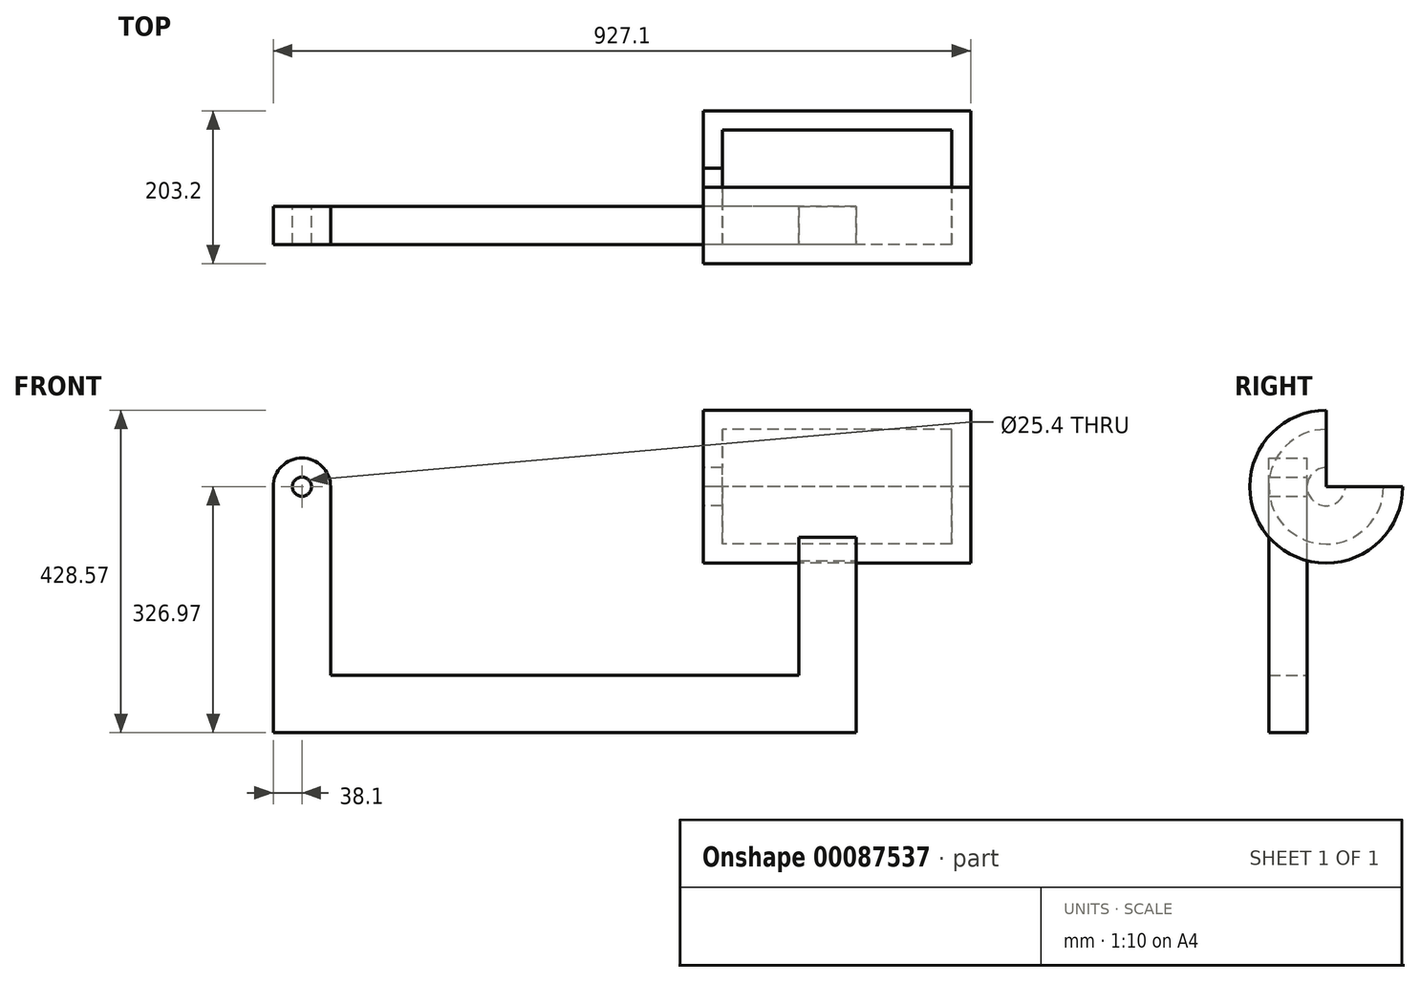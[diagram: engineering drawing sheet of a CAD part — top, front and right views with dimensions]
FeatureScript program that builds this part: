
annotation { "Feature Type Name" : "Feature", "Feature Type Description" : "" }
export const myFeature = defineFeature(function(context is Context, id is Id, definition is map)
    precondition{}
    {
        {
            var Q0;
            Q0=qCreatedBy(makeId("Front.planeOp"),FACE);
            var sketch = newSketch(context, id + "F0", { "sketchPlane" : qUnion([Q0])});
            skLineSegment(sketch, "E0", {"start": v(-165.1, 0) * mm, "end": v(165.1, 0) * mm, "construction": true});
            skLineSegment(sketch, "E1", {"start": v(165.1, 0) * mm, "end": v(165.1, 76.2) * mm});
            skLineSegment(sketch, "E2", {"start": v(165.1, 76.2) * mm, "end": v(-139.7, 76.2) * mm});
            skLineSegment(sketch, "E3", {"start": v(-139.7, 76.2) * mm, "end": v(-139.7, 25.4) * mm});
            skLineSegment(sketch, "E4", {"start": v(-139.7, 25.4) * mm, "end": v(-165.1, 25.4) * mm});
            skLineSegment(sketch, "E5", {"start": v(-165.1, 25.4) * mm, "end": v(-165.1, 101.6) * mm});
            skLineSegment(sketch, "E6", {"start": v(-165.1, 101.6) * mm, "end": v(190.5, 101.6) * mm});
            skLineSegment(sketch, "E7", {"start": v(190.5, 101.6) * mm, "end": v(190.5, 0) * mm});
            skLineSegment(sketch, "E8", {"start": v(190.5, 0) * mm, "end": v(165.1, 0) * mm});
            skLineSegment(sketch, "E9", {"start": v(-18.3, 101.6) * mm, "end": v(-18.3, 76.2) * mm, "construction": true});
            skLineSegment(sketch, "E10", {"start": v(-165.1, 25.4) * mm, "end": v(-165.1, -25.4) * mm, "construction": true});
            skSolve(sketch);
        }
        {
            var Q0;
            Q0=makeQuery(id+"F0.imprint","IMPRINT",FACE,{"disambiguationData":[TD([[makeQuery(id+"F0.imprint","IMPRINT",EDGE,{"derivedFrom":sQuery(id+"F0.wireOp",EDGE,"E1")}),-1.0]])]});
            var Q1;
            Q1=sQuery(id+"F0.wireOp",EDGE,"E0");
            revolve(context, id + "F1", {"entities" : qUnion([Q0]), "axis" : qUnion([Q1]), "revolveType" : RevolveType.FULL});
        }
        {
            var Q0;
            Q0=qCreatedBy(makeId("Front.planeOp"),FACE);
            cPlane(context, id + "F2", {"entities" : qUnion([Q0]), "cplaneType" : CPlaneType.OFFSET, "offset" : 25.4 * mm, "width" : 152.4 * mm, "height" : 152.4 * mm});
        }
        {
            var Q0;
            Q0=qCreatedBy(id+"F2.planeOp",FACE);
            var sketch = newSketch(context, id + "F3", { "sketchPlane" : qUnion([Q0])});
            skLineSegment(sketch, "E11", {"start": v(-165.1, -98.37) * mm, "end": v(190.5, -98.37) * mm, "construction": true});
            skLineSegment(sketch, "E12", {"start": v(190.5, 98.37) * mm, "end": v(-165.1, 98.37) * mm, "construction": true});
            skLineSegment(sketch, "E13.bottom", {"start": v(-38.1, -98.37) * mm, "end": v(38.1, -98.37) * mm});
            skLineSegment(sketch, "E13.left", {"start": v(-38.1, -98.37) * mm, "end": v(-38.1, -250.77) * mm});
            skLineSegment(sketch, "E13.right", {"start": v(38.1, -98.37) * mm, "end": v(38.1, -250.77) * mm});
            skLineSegment(sketch, "E14.bottom", {"start": v(-38.1, -250.77) * mm, "end": v(-660.4, -250.77) * mm});
            skLineSegment(sketch, "E14.top", {"start": v(38.1, -326.97) * mm, "end": v(-660.4, -326.97) * mm});
            skLineSegment(sketch, "E14.left", {"start": v(38.1, -250.77) * mm, "end": v(38.1, -326.97) * mm});
            skLineSegment(sketch, "E15.bottom", {"start": v(-660.4, -326.97) * mm, "end": v(-736.6, -326.97) * mm});
            skLineSegment(sketch, "E15.top", {"start": v(-698.5, 38.1) * mm, "end": v(-698.5, 38.1) * mm});
            skLineSegment(sketch, "E15.left", {"start": v(-660.4, -250.77) * mm, "end": v(-660.4, 0) * mm});
            skLineSegment(sketch, "E15.right", {"start": v(-736.6, -326.97) * mm, "end": v(-736.6, 0) * mm});
            skLineSegment(sketch, "E16", {"start": v(0, 0) * mm, "end": v(0, -98.37) * mm, "construction": true});
            skPoint(sketch, "E17.visualSharp", {"position": v(-736.6, 38.1) * mm});
            skArc(sketch, "E17.filletArc", {"start": v(-698.5, 38.1) * mm, "mid": v(-725.44, 26.94) * mm, "end": v(-736.6, 0) * mm});
            skPoint(sketch, "E18.visualSharp", {"position": v(-660.4, 38.1) * mm});
            skArc(sketch, "E18.filletArc", {"start": v(-660.4, 0) * mm, "mid": v(-671.56, 26.94) * mm, "end": v(-698.5, 38.1) * mm});
            skCircle(sketch, "E19", {"center": v(-698.5, 0) * mm, "radius": 12.7 * mm});
            skLineSegment(sketch, "E20", {"start": v(-698.5, 0) * mm, "end": v(0, 0) * mm, "construction": true});
            skCircle(sketch, "E21", {"center": v(-698.5, 0) * mm, "radius": 152.4 * mm, "construction": true});
            skCircle(sketch, "E22", {"center": v(-698.5, 0) * mm, "radius": 127 * mm, "construction": true});
            skLineSegment(sketch, "E23", {"start": v(114.3, 0) * mm, "end": v(-215.9, 0) * mm, "construction": true});
            skLineSegment(sketch, "E24", {"start": v(-215.9, 0) * mm, "end": v(-571.5, 0) * mm, "construction": true});
            skSolve(sketch);
        }
        {
            var Q0;
            Q0=makeQuery(id+"F3.imprint","IMPRINT",FACE,{"disambiguationData":[TD([[makeQuery(id+"F3.imprint","IMPRINT",EDGE,{"derivedFrom":sQuery(id+"F3.wireOp",EDGE,"E13.bottom")}),-1.0]])]});
            extrude(context, id + "F4", {"entities" : qUnion([Q0]), "depth" : 50.8 * mm});
        }
        {
            var Q0;
            Q0=makeQuery(id+"F4.opExtrude","SWEPT_FACE",FACE,{"disambiguationData":[OSD([sQuery(id+"F3.wireOp",EDGE,"E13.bottom")])]});
            var Q1;
            Q1=makeQuery(id+"F1.opRevolve","SWEPT_BODY",BODY,{"disambiguationData":[OSD([sQuery(id+"F0.wireOp",EDGE,"E1"),sQuery(id+"F0.wireOp",EDGE,"E2"),sQuery(id+"F0.wireOp",EDGE,"E3"),sQuery(id+"F0.wireOp",EDGE,"E4"),sQuery(id+"F0.wireOp",EDGE,"E5"),sQuery(id+"F0.wireOp",EDGE,"E6"),sQuery(id+"F0.wireOp",EDGE,"E7"),sQuery(id+"F0.wireOp",EDGE,"E8")])]});
            extrude(context, id + "F5", {"entities" : qUnion([Q0]), "operationType" : NewBodyOperationType.ADD, "endBound" : BoundingType.UP_TO_BODY, "endBoundEntityBody" : qUnion([Q1]), "depth" : 25.4 * mm});
        }
        {
            var Q0;
            Q0=makeQuery(id+"F1.opRevolve","SWEPT_FACE",FACE,{"disambiguationData":[OSD([sQuery(id+"F0.wireOp",EDGE,"E5")])]});
            var sketch = newSketch(context, id + "F6", { "sketchPlane" : qUnion([Q0])});
            skLineSegment(sketch, "E25.bottom", {"start": v(0, 0) * mm, "end": v(-218.92, 0) * mm});
            skLineSegment(sketch, "E25.top", {"start": v(0, 225.13) * mm, "end": v(-218.92, 225.13) * mm});
            skLineSegment(sketch, "E25.left", {"start": v(0, 0) * mm, "end": v(0, 225.13) * mm});
            skLineSegment(sketch, "E25.right", {"start": v(-218.92, 0) * mm, "end": v(-218.92, 225.13) * mm});
            skSolve(sketch);
        }
        {
            var Q0;
            Q0 = qSketchRegion(id + "F6", true);
            extrude(context, id + "F7", {"entities" : qUnion([Q0]), "operationType" : NewBodyOperationType.REMOVE, "oppositeDirection" : true, "depth" : 723.2 * mm});
        }
    });
